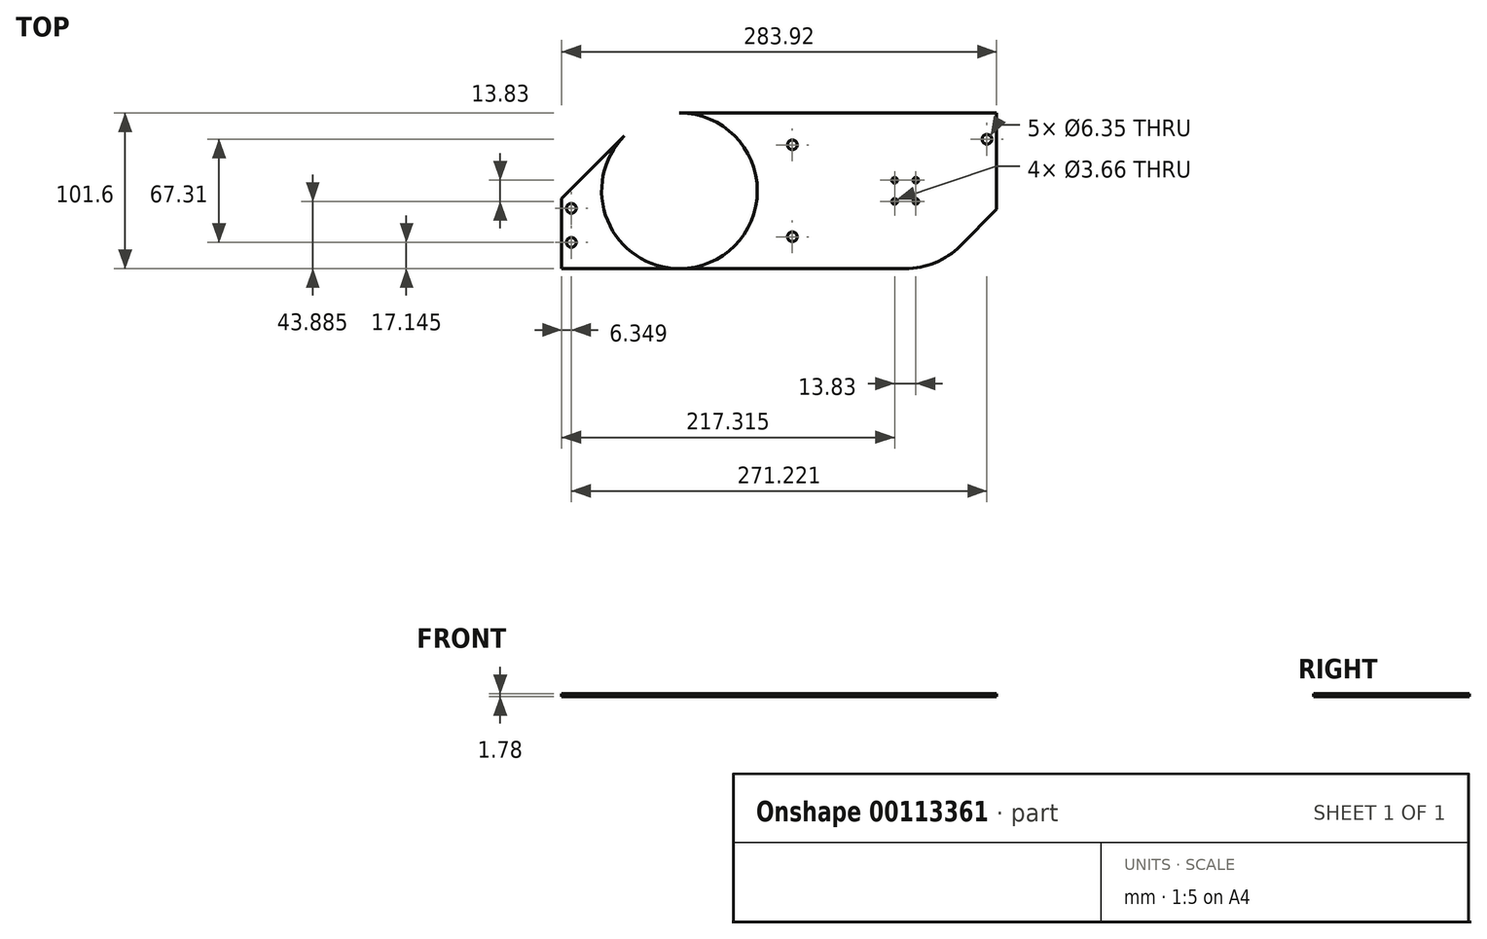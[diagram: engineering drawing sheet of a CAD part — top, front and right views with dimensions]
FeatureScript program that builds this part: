
annotation { "Feature Type Name" : "Feature", "Feature Type Description" : "" }
export const myFeature = defineFeature(function(context is Context, id is Id, definition is map)
    precondition{}
    {
        {
            var Q0;
            Q0=qCreatedBy(makeId("Top.planeOp"),FACE);
            var sketch = newSketch(context, id + "F0", { "sketchPlane" : qUnion([Q0])});
            skLineSegment(sketch, "E0.bottom", {"start": v(133.35, 50.8) * mm, "end": v(-133.35, 50.8) * mm});
            skLineSegment(sketch, "E0.top", {"start": v(133.35, -50.8) * mm, "end": v(-133.35, -50.8) * mm});
            skLineSegment(sketch, "E0.left", {"start": v(133.35, 50.8) * mm, "end": v(133.35, -50.8) * mm});
            skLineSegment(sketch, "E0.right", {"start": v(-133.35, 50.8) * mm, "end": v(-133.35, -50.8) * mm});
            skPoint(sketch, "E0.middle", {"position": v(0, 0) * mm});
            skCircle(sketch, "E1", {"center": v(73.66, 0) * mm, "radius": 9.78 * mm, "construction": true});
            skCircle(sketch, "E2", {"center": v(-73.66, 0) * mm, "radius": 25.4 * mm, "construction": true});
            skCircle(sketch, "E3", {"center": v(-73.66, 0) * mm, "radius": 50.8 * mm});
            skCircle(sketch, "E4", {"center": v(-73.66, 0) * mm, "radius": 53.98 * mm, "construction": true});
            skCircle(sketch, "E5", {"center": v(73.66, 0) * mm, "radius": 53.98 * mm, "construction": true});
            skCircle(sketch, "E6", {"center": v(73.66, 0) * mm, "radius": 50.8 * mm});
            skCircle(sketch, "E7", {"center": v(-254, 41.73) * mm, "radius": 12.7 * mm, "construction": true});
            skCircle(sketch, "E8", {"center": v(0, 29.97) * mm, "radius": 15.24 * mm, "construction": true});
            skCircle(sketch, "E9", {"center": v(-254, -40.97) * mm, "radius": 12.7 * mm, "construction": true});
            skCircle(sketch, "E10", {"center": v(0, -29.97) * mm, "radius": 15.24 * mm, "construction": true});
            skCircle(sketch, "E11", {"center": v(-73.66, 0) * mm, "radius": 45.21 * mm, "construction": true});
            skCircle(sketch, "E12", {"center": v(73.66, 0) * mm, "radius": 45.21 * mm, "construction": true});
            skLineSegment(sketch, "E13", {"start": v(-73.66, 45.21) * mm, "end": v(73.66, 45.21) * mm, "construction": true});
            skLineSegment(sketch, "E14", {"start": v(-73.66, -45.21) * mm, "end": v(73.66, -45.21) * mm, "construction": true});
            skCircle(sketch, "E15", {"center": v(0, 29.97) * mm, "radius": 3.18 * mm});
            skCircle(sketch, "E16", {"center": v(0, -29.97) * mm, "radius": 3.18 * mm});
            skLineSegment(sketch, "E17", {"start": v(73.66, 0) * mm, "end": v(73.66, 9.78) * mm, "construction": true});
            skLineSegment(sketch, "E18", {"start": v(66.75, 6.91) * mm, "end": v(80.57, -6.91) * mm, "construction": true});
            skLineSegment(sketch, "E19", {"start": v(66.75, -6.91) * mm, "end": v(80.57, 6.91) * mm, "construction": true});
            skCircle(sketch, "E20", {"center": v(66.75, 6.91) * mm, "radius": 1.83 * mm});
            skCircle(sketch, "E21", {"center": v(80.57, 6.91) * mm, "radius": 1.83 * mm});
            skCircle(sketch, "E22", {"center": v(66.75, -6.91) * mm, "radius": 1.83 * mm});
            skCircle(sketch, "E23", {"center": v(80.57, -6.91) * mm, "radius": 1.83 * mm});
            skLineSegment(sketch, "E24", {"start": v(-133.35, 12.15) * mm, "end": v(-109.58, 35.92) * mm});
            skLineSegment(sketch, "E25", {"start": v(109.58, -35.92) * mm, "end": v(133.35, -12.15) * mm});
            skCircle(sketch, "E26", {"center": v(-144.22, -33.66) * mm, "radius": 3.18 * mm});
            skCircle(sketch, "E27", {"center": v(127, 33.66) * mm, "radius": 3.18 * mm});
            skCircle(sketch, "E28", {"center": v(-144.22, -33.66) * mm, "radius": 6.99 * mm, "construction": true});
            skCircle(sketch, "E29", {"center": v(127, 33.66) * mm, "radius": 6.99 * mm, "construction": true});
            skLineSegment(sketch, "E30", {"start": v(-109.58, 35.92) * mm, "end": v(-196.3, -50.8) * mm, "construction": true});
            skLineSegment(sketch, "E31", {"start": v(-196.3, -50.8) * mm, "end": v(-133.35, -50.8) * mm, "construction": true});
            skLineSegment(sketch, "E32", {"start": v(109.58, -35.92) * mm, "end": v(196.3, 50.8) * mm, "construction": true});
            skLineSegment(sketch, "E33", {"start": v(196.3, 50.8) * mm, "end": v(133.35, 50.8) * mm, "construction": true});
            skCircle(sketch, "E34", {"center": v(-73.66, 15.88) * mm, "radius": 1.83 * mm});
            skCircle(sketch, "E35", {"center": v(-73.66, -15.88) * mm, "radius": 1.83 * mm});
            skLineSegment(sketch, "E36", {"start": v(-150.57, -50.8) * mm, "end": v(-150.57, -5.07) * mm});
            skLineSegment(sketch, "E37", {"start": v(-150.57, -5.07) * mm, "end": v(-133.35, 12.15) * mm});
            skLineSegment(sketch, "E38", {"start": v(-133.35, -50.8) * mm, "end": v(-150.57, -50.8) * mm});
            skCircle(sketch, "E39", {"center": v(-144.22, -11.43) * mm, "radius": 3.18 * mm});
            skCircle(sketch, "E40", {"center": v(-144.22, -11.43) * mm, "radius": 6.99 * mm, "construction": true});
            skPoint(sketch, "E41", {"position": v(-128.7, 16.8) * mm});
            skSolve(sketch);
        }
        {
            var Q0;
            {var subQ4=sQuery(id+"F0.wireOp",EDGE,"E25");Q0=makeQuery(id+"F0.imprint","IMPRINT",FACE,{"disambiguationData":[TD([[makeQuery(id+"F0.imprint","IMPRINT",EDGE,{"derivedFrom":subQ4}),1.0]])]});}
            var Q1;
            Q1=makeQuery(id+"F0.imprint","IMPRINT",FACE,{"disambiguationData":[TD([[makeQuery(id+"F0.imprint","IMPRINT",EDGE,{"derivedFrom":sQuery(id+"F0.wireOp",EDGE,"E20")}),-1.0]])]});
            var Q2;
            Q2=makeQuery(id+"F0.imprint","IMPRINT",FACE,{"disambiguationData":[TD([[makeQuery(id+"F0.imprint","IMPRINT",EDGE,{"derivedFrom":sQuery(id+"F0.wireOp",EDGE,"E15")}),-1.0]])]});
            var Q3;
            {var subQ0=sQuery(id+"F0.wireOp",EDGE,"E3");var subQ1=makeQuery(id+"F0.imprint","IMPRINT",VERTEX,{"derivedFrom":subQ0});Q3=makeQuery(id+"F0.imprint","IMPRINT",FACE,{"disambiguationData":[TD([[makeQuery(id+"F0.imprint","IMPRINT",EDGE,{"disambiguationData":[TD([[subQ1,-1.0]])],"derivedFrom":subQ0}),1.0]])]});}
            var Q4;
            {var subQ5=sQuery(id+"F0.wireOp",EDGE,"E24");Q4=makeQuery(id+"F0.imprint","IMPRINT",FACE,{"disambiguationData":[TD([[makeQuery(id+"F0.imprint","IMPRINT",EDGE,{"derivedFrom":subQ5}),-1.0]])]});}
            var Q5;
            Q5=makeQuery(id+"F0.imprint","IMPRINT",FACE,{"disambiguationData":[TD([[makeQuery(id+"F0.imprint","IMPRINT",EDGE,{"derivedFrom":sQuery(id+"F0.wireOp",EDGE,"E26")}),-1.0]])]});
            extrude(context, id + "F1", {"entities" : qUnion([Q0, Q1, Q2, Q3, Q4, Q5]), "depth" : 1.78 * mm, "offsetDistance" : 25.4 * mm});
        }
    });
